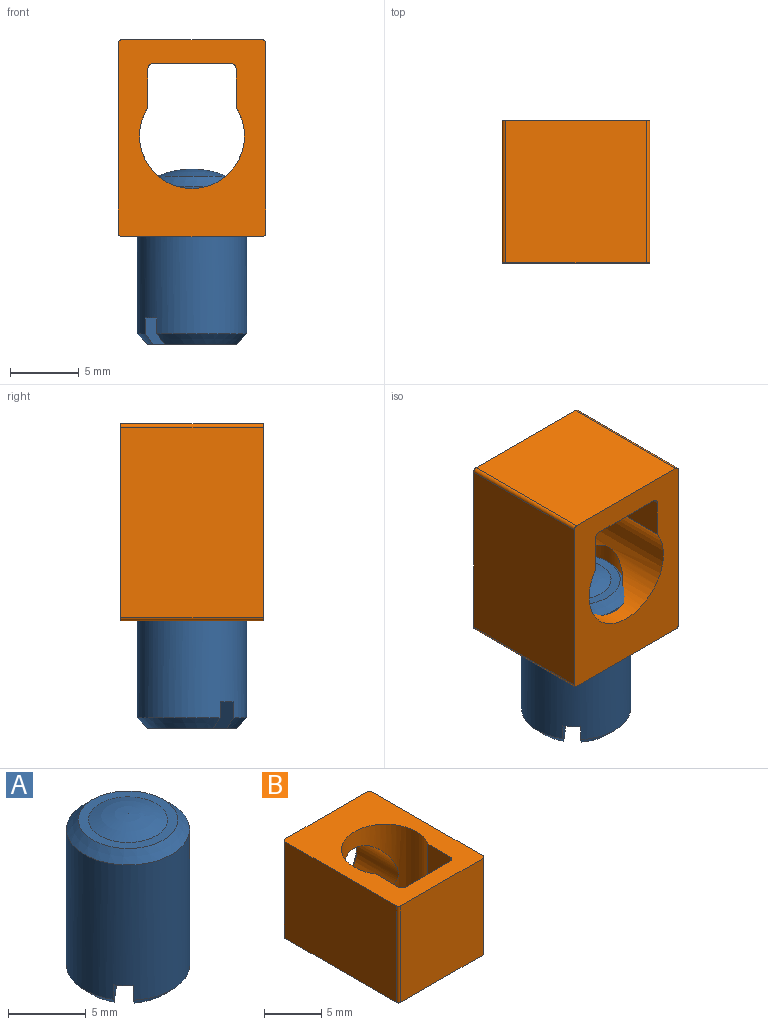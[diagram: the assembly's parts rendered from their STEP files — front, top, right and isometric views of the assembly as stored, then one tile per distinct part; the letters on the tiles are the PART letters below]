
ASSEMBLY  parts=2 mates=1
PART A: 11 faces, bbox 7.9x7.9x12.7 mm
  f0: cone r=3.58mm half-angle=45deg, axis (0,0,-1), area 24.2mm2, adj f1,f2
  f1: cylinder r=3.96mm len=10.66mm, axis (0,0,1), area 262.5mm2, adj f0,f3,f4,f5,f7,f8
  f2: plane 6.4x6.4mm, normal (0,0,1), area 11.9mm2, adj f0,f6
  f3: cone r=3.58mm half-angle=45deg, axis (0,0,1), area 10.7mm2, adj f1,f4,f9
  f4: plane 5.96x5.07mm, normal (-0.65,0.76,0), area 14.3mm2, adj f1,f3,f8,f9
  f5: cone r=3.58mm half-angle=45deg, axis (0,0,1), area 10.7mm2, adj f1,f7,f10
  f6: sphere r=6.54mm, area 21.1mm2, adj f2
  f7: plane 5.96x5.07mm, normal (0.65,-0.76,0), area 14.3mm2, adj f1,f5,f8,f10
  f8: plane 6.8x6.05mm, normal (0,0,-1), area 10.2mm2, adj f1,f4,f7
  f9: plane 5.17x4.74mm, normal (0,0,-1), area 12mm2, adj f3,f4
  f10: plane 5.17x4.74mm, normal (0,0,-1), area 12mm2, adj f5,f7
PART B: 25 faces, bbox 10.7x14.3x10.3 mm
  f0: cylinder r=0.25mm len=10.31mm, axis (0,0,1), area 4.1mm2, adj f1,f2,f23,f24
  f1: plane 13.77x10.31mm, normal (1,0,0), area 142mm2, adj f0,f2,f3,f24
  f2: plane 14.28x10.69mm, normal (0,0,-1), area 94.5mm2, adj f0,f1,f3,f4,f5,f6,f7,f16
  f3: cylinder r=0.25mm len=10.31mm, axis (0,0,1), area 4.1mm2, adj f1,f2,f4,f24
  f4: plane 10.31x10.19mm, normal (0,1,0), area 60.3mm2, adj f2,f3,f5,f8,f24
  f5: cylinder r=0.25mm len=10.31mm, axis (0,0,1), area 4.1mm2, adj f2,f4,f6,f24
  f6: plane 13.77x10.31mm, normal (-1,0,0), area 142mm2, adj f2,f5,f7,f24
  f7: cylinder r=0.25mm len=10.31mm, axis (0,0,1), area 4.1mm2, adj f2,f6,f23,f24
  f8: cone r=3.58mm half-angle=45deg, axis (0,1,0), area 12.1mm2, adj f4,f9
  f9: cylinder r=3.39mm len=6.78mm, axis (0,1,0), area 86.2mm2, adj f8,f18
  f10: cone r=1.7mm half-angle=85deg, axis (0,1,0), area 0mm2, adj f12,f16
  f11: cone r=1.7mm half-angle=85deg, axis (0,1,0), area 1.9mm2, adj f19
  f12: cylinder r=3.39mm len=3.29mm, axis (0,1,0), area 7.3mm2, adj f10,f16,f17,f18,f22
  f13: cylinder r=3.39mm len=3.29mm, axis (0,1,0), area 7.3mm2, adj f14,f15,f18,f20,f21
  f14: cone r=1.7mm half-angle=85deg, axis (0,1,0), area 0mm2, adj f13,f20
  f15: plane 4.04x2.81mm, normal (-1,0,0), area 11.3mm2, adj f13,f18,f20,f24
  f16: cylinder r=0.38mm len=10.31mm, axis (0,0,-1), area 5.8mm2, adj f2,f10,f12,f17,f19,f22,f24
  f17: plane 4.04x2.81mm, normal (1,0,0), area 11.3mm2, adj f12,f16,f18,f24
  f18: cylinder r=3.81mm len=10.31mm, axis (0,0,-1), area 125.9mm2, adj f2,f9,f12,f13,f15,f17,f21,f22
  f19: plane 10.31x5.64mm, normal (0,1,0), area 56.2mm2, adj f2,f11,f16,f20,f24
  f20: cylinder r=0.38mm len=10.31mm, axis (0,0,-1), area 5.8mm2, adj f2,f13,f14,f15,f19,f21,f24
  f21: plane 4.04x2.81mm, normal (-1,0,0), area 11.3mm2, adj f2,f13,f18,f20
  f22: plane 4.04x2.81mm, normal (1,0,0), area 11.3mm2, adj f2,f12,f16,f18
  f23: plane 10.31x10.19mm, normal (0,-1,0), area 105mm2, adj f0,f2,f7,f24
  f24: plane 14.28x10.69mm, normal (0,0,1), area 94.5mm2, adj f0,f1,f3,f4,f5,f6,f7,f15
PLACE A t=(13.4,-1.61,-9.89)mm
PLACE B rot(axis=(-1,0,0),90deg) t=(13.4,69.43,-5.43)mm
MATE cylindrical B.f8 <-> A.f0  axis (0,0,-1) through (13.4,-1.61,-12.19)mm
